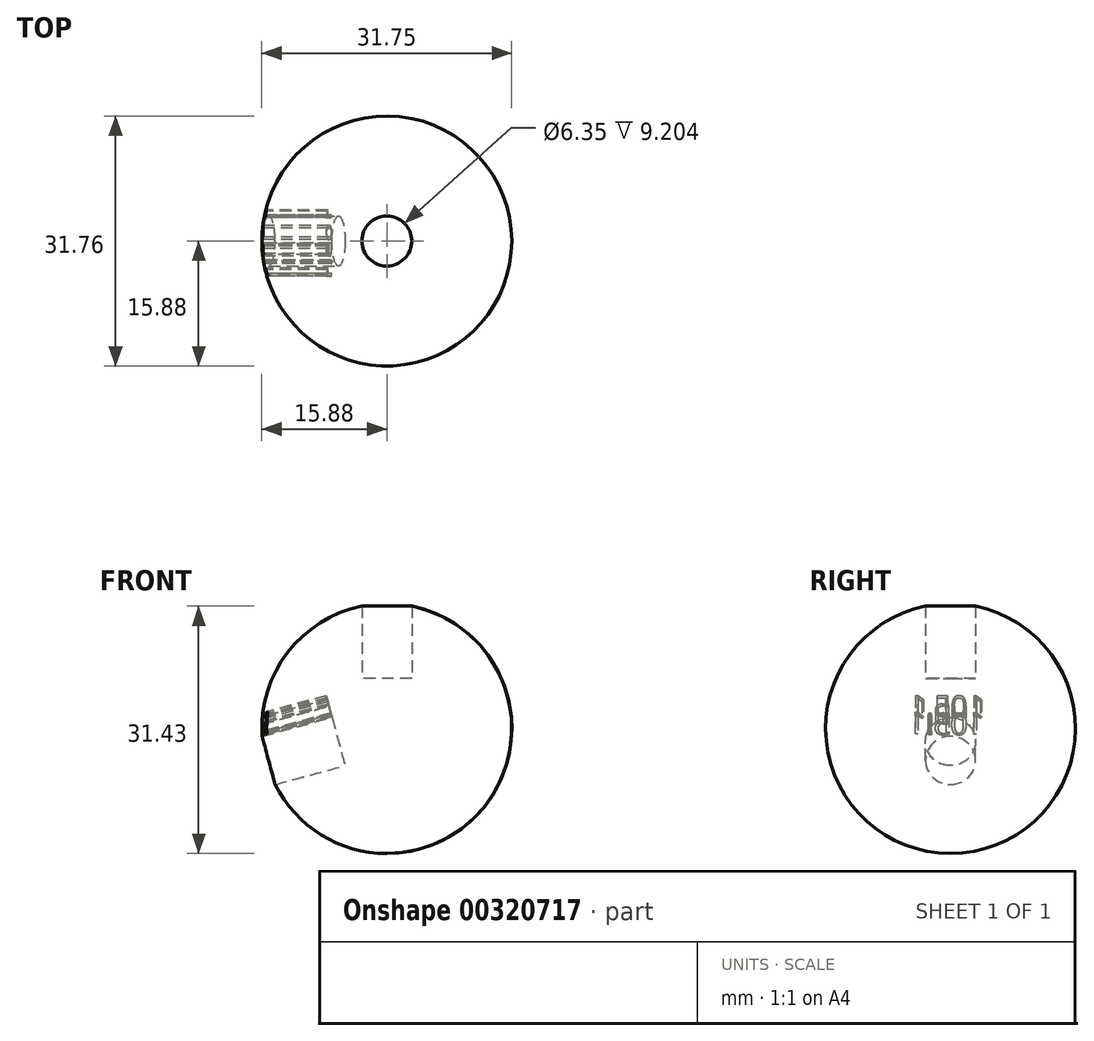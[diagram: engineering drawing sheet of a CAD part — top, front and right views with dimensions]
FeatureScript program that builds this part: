
annotation { "Feature Type Name" : "Feature", "Feature Type Description" : "" }
export const myFeature = defineFeature(function(context is Context, id is Id, definition is map)
    precondition{}
    {
        {
            var Q0;
            Q0=qCreatedBy(makeId("Front.planeOp"),FACE);
            var sketch = newSketch(context, id + "F0", { "sketchPlane" : qUnion([Q0])});
            skArc(sketch, "E0", {"start": v(0, 15.88) * mm, "mid": v(-15.88, 0) * mm, "end": v(0, -15.88) * mm});
            skLineSegment(sketch, "E1", {"start": v(0, 15.88) * mm, "end": v(0, -15.88) * mm});
            skSolve(sketch);
        }
        {
            var Q0;
            Q0=qCreatedBy(makeId("Top.planeOp"),FACE);
            var sketch = newSketch(context, id + "F1", { "sketchPlane" : qUnion([Q0])});
            skCircle(sketch, "E2", {"center": v(0, 0) * mm, "radius": 15.88 * mm});
            skSolve(sketch);
        }
        {
            var Q0;
            Q0=makeQuery(id+"F0.imprint","IMPRINT",FACE,{"disambiguationData":[TD([[makeQuery(id+"F0.imprint","IMPRINT",EDGE,{"derivedFrom":sQuery(id+"F0.wireOp",EDGE,"E0")}),1.0]])]});
            var Q1;
            Q1=sQuery(id+"F1.wireOp",EDGE,"E2");
            revolve(context, id + "F2", {"entities" : qUnion([Q0]), "axis" : qUnion([Q1]), "revolveType" : RevolveType.FULL});
        }
        {
            var Q0;
            Q0=qCreatedBy(makeId("Top.planeOp"),FACE);
            cPlane(context, id + "F3", {"entities" : qUnion([Q0]), "cplaneType" : CPlaneType.OFFSET, "offset" : 6.35 * mm, "width" : 152.4 * mm, "height" : 152.4 * mm});
        }
        {
            var Q0;
            Q0=qCreatedBy(id+"F3.planeOp",FACE);
            var sketch = newSketch(context, id + "F4", { "sketchPlane" : qUnion([Q0])});
            skCircle(sketch, "E3", {"center": v(0, 0) * mm, "radius": 3.18 * mm});
            skSolve(sketch);
        }
        {
            var Q0;
            Q0=qSketchRegion(id+"F4",true);
            extrude(context, id + "F5", {"entities" : qUnion([Q0]), "depth" : 50.8 * mm});
        }
        {
            var Q0;
            Q0=qCreatedBy(makeId("Right.planeOp"),FACE);
            var sketch = newSketch(context, id + "F6", { "sketchPlane" : qUnion([Q0])});
            skLineSegment(sketch, "E4", {"start": v(0, 0) * mm, "end": v(-59.73, 0) * mm, "construction": true});
            skSolve(sketch);
        }
        {
            var Q0;
            Q0=makeQuery(id+"F5.opExtrude","SWEPT_BODY",BODY,{"disambiguationData":[OSD([sQuery(id+"F4.wireOp",EDGE,"E3")])]});
            var Q1;
            Q1=sQuery(id+"F6.wireOp",EDGE,"E4");
            transform(context, id + "F7", {"entities" : qUnion([Q0]), "transformType" : TransformType.ROTATION, "transformAxis" : qUnion([Q1]), "angle" : 105.1 * degree, "makeCopy" : true});
        }
        {
            var Q0;
            Q0=makeQuery(id+"F7.opPattern","COPY",FACE,{"derivedFrom":makeQuery(id+"F5.opExtrude","CAP_FACE",FACE,{"disambiguationData":[OSD([sQuery(id+"F4.wireOp",EDGE,"E3")])],"isStart":false}),"instanceName":"1"});
            cPlane(context, id + "F8", {"entities" : qUnion([Q0]), "cplaneType" : CPlaneType.OFFSET, "offset" : 31.75 * mm, "oppositeDirection" : true, "width" : 152.4 * mm, "height" : 152.4 * mm});
        }
        {
            var Q0;
            Q0=qCreatedBy(id+"F8.planeOp",FACE);
            var sketch = newSketch(context, id + "F9", { "sketchPlane" : qUnion([Q0])});
            skText(sketch, "E5", { "text": "105.1\n", "fontName": "OpenSans-Regular.ttf"});
            const initialGuessF9  = {"E5": [-0.00428, 0.00332, 1, 0, 0.00269]};
            skSetInitialGuess(sketch, initialGuessF9);
            skSolve(sketch);
        }
        {
            var Q0;
            Q0=qSketchRegion(id+"F9",true);
            extrude(context, id + "F10", {"entities" : qUnion([Q0]), "operationType" : NewBodyOperationType.REMOVE, "oppositeDirection" : true, "depth" : 19.05 * mm});
        }
        {
            var Q0;
            Q0=makeQuery(id+"F5.opExtrude","SWEPT_BODY",BODY,{"disambiguationData":[OSD([sQuery(id+"F4.wireOp",EDGE,"E3")])]});
            var Q1;
            Q1=makeQuery(id+"F7.opPattern","COPY",BODY,{"derivedFrom":makeQuery(id+"F5.opExtrude","SWEPT_BODY",BODY,{"disambiguationData":[OSD([sQuery(id+"F4.wireOp",EDGE,"E3")])]}),"instanceName":"1"});
            var Q2;
            Q2=makeQuery(id+"F2.opRevolve","SWEPT_BODY",BODY,{"disambiguationData":[OSD([sQuery(id+"F0.wireOp",EDGE,"E0"),sQuery(id+"F0.wireOp",EDGE,"E1")])]});
            booleanBodies(context, id + "F11", {"operationType" : BooleanOperationType.SUBTRACTION, "tools" : qUnion([Q0, Q1]), "targets" : qUnion([Q2])});
        }
    });
